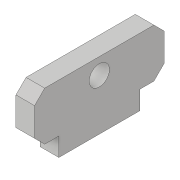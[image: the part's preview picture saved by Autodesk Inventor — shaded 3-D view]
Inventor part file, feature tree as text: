
AUTODESK INVENTOR PART (.ipt)
format: ipt  version: 2017 (Build 210142000, 142)  size: 98,304 bytes
history: native  units: in
note: dims shown in document units (in); Inventor stores cm internally (conversion verified against a paired STEP export)
features: extrude x2, sketch x2, chamfer x1
ambient origin geometry x8: Origin, YZ Plane, XZ Plane, XY Plane, X Axis, Y Axis, Z Axis, Center Point
bodies: Solid1 (feature_tree)
feature tree (5):
  extrude  "Extrusion1"  Depth=0.115in
  extrude  "Extrusion2"  Depth=0.4in
  chamfer  "Chamfer1"  Distance=0.15in
  sketch  "Sketch1"  dims[d0=0.5in d1=0.115in]
  sketch  "Sketch2"  dims[d2=0.8in d3=0.4in d4=0.15in d5=0.3in d6=0.115in d7=0.0in d8=0.125in d9=0.2in d10=0.115in d11=0.0in d12=0.0625in d13=0.125in d14=45.0deg]
